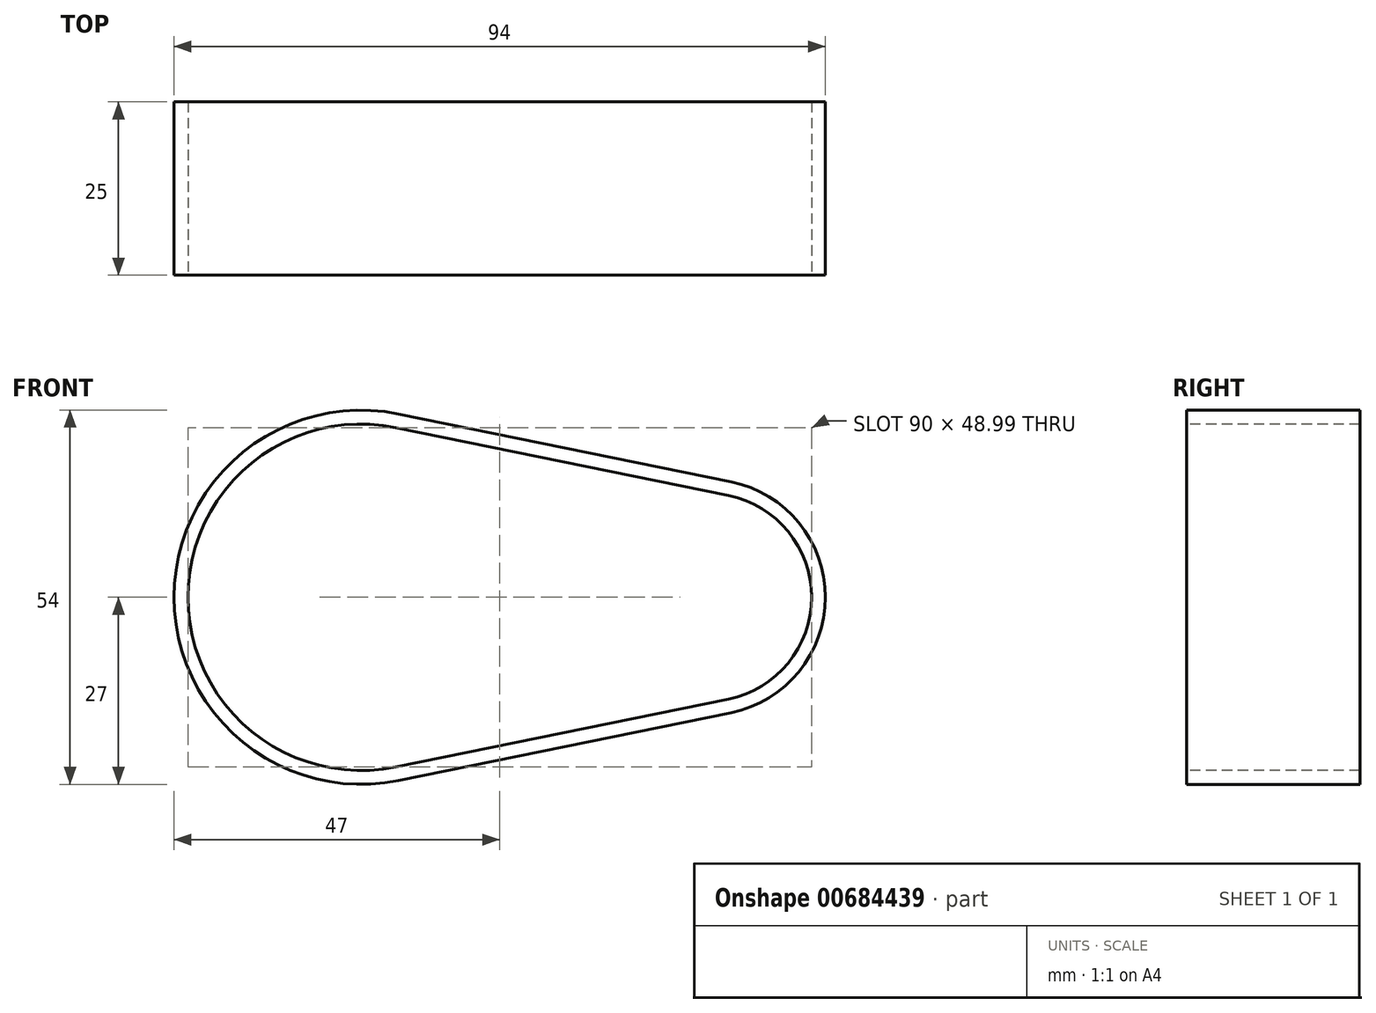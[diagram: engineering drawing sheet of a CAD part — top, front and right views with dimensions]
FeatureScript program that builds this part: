
annotation { "Feature Type Name" : "Feature", "Feature Type Description" : "" }
export const myFeature = defineFeature(function(context is Context, id is Id, definition is map)
    precondition{}
    {
        {
            var Q0;
            Q0=qCreatedBy(makeId("Front.planeOp"),FACE);
            var sketch = newSketch(context, id + "F0", { "sketchPlane" : qUnion([Q0])});
            skCircle(sketch, "E0", {"center": v(0, 0) * mm, "radius": 15 * mm});
            skCircle(sketch, "E1", {"center": v(-50, 0) * mm, "radius": 25 * mm});
            skLineSegment(sketch, "E2", {"start": v(-50, 0) * mm, "end": v(0, 0) * mm, "construction": true});
            skLineSegment(sketch, "E3", {"start": v(-45, 24.5) * mm, "end": v(0, 15.3) * mm});
            skLineSegment(sketch, "E4", {"start": v(0, -15.3) * mm, "end": v(-45, -24.5) * mm});
            skArc(sketch, "E5.0", {"start": v(-4.84, -16.3) * mm, "mid": v(17, 0) * mm, "end": v(-4.84, 16.3) * mm});
            skCircle(sketch, "E6.0", {"center": v(-50, 0) * mm, "radius": 27 * mm});
            skLineSegment(sketch, "E7", {"start": v(3.4, 16.66) * mm, "end": v(-44.6, 26.45) * mm});
            skLineSegment(sketch, "E8", {"start": v(-44.6, -26.45) * mm, "end": v(3.4, -16.66) * mm});
            skPoint(sketch, "E9", {"position": v(-4.84, 16.3) * mm});
            skPoint(sketch, "E10", {"position": v(-4.84, -16.3) * mm});
            skPoint(sketch, "E11", {"position": v(0, -15.3) * mm});
            skPoint(sketch, "E12", {"position": v(0, 15.3) * mm});
            skLineSegment(sketch, "E13", {"start": v(0, 15.3) * mm, "end": v(0, -15.3) * mm, "construction": true});
            skSolve(sketch);
        }
        {
            var Q0;
            Q0 = qSketchRegion(id + "F0", true);
            var Q1;
            {var subQ0=sQuery(id+"F0.wireOp",EDGE,"E1");var subQ1=makeQuery(id+"F0.imprint","INTERSECT",VERTEX,{"derivedFrom":[subQ0,sQuery(id+"F0.wireOp",EDGE,"E3")]});Q1=makeQuery(id+"F0.imprint","IMPRINT",FACE,{"disambiguationData":[TD([[makeQuery(id+"F0.imprint","IMPRINT",EDGE,{"disambiguationData":[TD([[subQ1,-1.0]])],"derivedFrom":subQ0}),1.0]])]});}
            var Q2;
            {var subQ0=sQuery(id+"F0.wireOp",EDGE,"E3");var subQ1=sQuery(id+"F0.wireOp",EDGE,"E1");var subQ2=makeQuery(id+"F0.imprint","INTERSECT",VERTEX,{"derivedFrom":[subQ1,subQ0]});Q2=makeQuery(id+"F0.imprint","IMPRINT",FACE,{"disambiguationData":[TD([[makeQuery(id+"F0.imprint","IMPRINT",EDGE,{"disambiguationData":[TD([[subQ2,1.0]])],"derivedFrom":subQ1}),-1.0]])]});}
            var Q3;
            Q3=makeQuery(id+"F0.imprint","IMPRINT",FACE,{"disambiguationData":[TD([[makeQuery(id+"F0.imprint","IMPRINT",EDGE,{"derivedFrom":sQuery(id+"F0.wireOp",EDGE,"E0")}),1.0]])]});
            extrude(context, id + "F1", {"entities" : qUnion([Q0, Q1, Q2, Q3]), "depth" : 25 * mm, "offsetDistance" : 25 * mm});
        }
        {
            var Q0;
            Q0=makeQuery(id+"F1.opExtrude","CAP_FACE",FACE,{"disambiguationData":[OSD([sQuery(id+"F0.wireOp",EDGE,"E5.0"),sQuery(id+"F0.wireOp",EDGE,"E6.0"),sQuery(id+"F0.wireOp",EDGE,"E7"),sQuery(id+"F0.wireOp",EDGE,"E8")])],"isStart":false});
            var sketch = newSketch(context, id + "F2", { "sketchPlane" : qUnion([Q0])});
            skLineSegment(sketch, "E14.0", {"start": v(3, 14.7) * mm, "end": v(-45, 24.5) * mm});
            skArc(sketch, "E14.1", {"start": v(3, -14.7) * mm, "mid": v(15, 0) * mm, "end": v(3, 14.7) * mm});
            skLineSegment(sketch, "E14.2", {"start": v(-45, -24.5) * mm, "end": v(3, -14.7) * mm});
            skArc(sketch, "E14.3", {"start": v(-45, 24.5) * mm, "mid": v(-75, 0) * mm, "end": v(-45, -24.5) * mm});
            skSolve(sketch);
        }
        {
            var Q0;
            Q0 = qSketchRegion(id + "F2", true);
            extrude(context, id + "F3", {"entities" : qUnion([Q0]), "operationType" : NewBodyOperationType.REMOVE, "endBound" : BoundingType.THROUGH_ALL, "oppositeDirection" : true, "depth" : 25 * mm, "offsetDistance" : 25 * mm});
        }
    });
